# Revit family: Electronics -Communication_Urmet_1760-6
name_source: partatom
category: Apparecchi elettrici
revit_build: Autodesk Revit 2017 (Build: 20190508_0315(x64)
units: mm (PartAtom-declared; Revit-internal decimal feet)

## family parameters
Condiviso = No
Host = Superficie
Mantenere orientamento annotazione = No
Punto di calcolo locali = No
Quota connettore circolare = Usa diametro
Taglio con vuoti quando caricato = No
Tipo di parte = Normale

## types (1)
- Electronics -Communication_Urmet_1760-6
    Additional led signalizations = 0
    Audio or Audio/Video system = Audio/video
    Auto-insertion function and scrolling of CCTV cameras = Sì
    Automatic door opening function = Sì
    Auxiliary antenna for Hearing impaired people = Sì
    Brand url = https://www.urmet.com
    Call forwarding = Yes, with optional device
    Codice assieme = 1760/6
    Color = White RAL9003
    Combined Nomenclature Code = 8517691000
    Compatibility with Alexa = No
    Data-sheet: = http://qrcode.urmet.com
    Date of publishing = 2023-02-01
    Descrizione = VIDEO DOOR PHONE HANDS-FREE
VIDEO HOUSEPHONE 4,3'’ HANDSFREE 2VOICE WHITE
    Design country = Italy
    Dimensions (LxHxP) = 130 x 160 x 26 mm
    Display Dimensions = 5’’ IPS-LCD
    Display Format = 16:9
    Display resolution (pixel) = 800 x 480
    EAN Product Code = 8021156069781
    Edition number = 1
    Finishing = Gloss
    Gate door opening = Sì
    Gesture = Sì
    Handset /Hands free = Hands free
    Home automation Yokis buttons = -
    Humidity range (%) = 95%
    IFC Classification = Electrical Element
    IK Grade = -
    IP Grade = 30
    Incoming floor call = Sì
    Installation = Surface mounting, flush mounting or table mounting (with optional accessory)
    Installation instructions = http://qrcode.urmet.com
    Installation on 503 flush and 60 mm diameter round boxes = Sì
    Main led signalizations = 5
    Manufacturer country = China
    Masterformat 2014 Code = 27 51 23.30
    Masterformat 2014 Description = Residential Intercommunications and Program Systems
    Material main = Plastic
    Modello = VOG5
    N. od terminal blocks = 6
    NBS Reference Code = 16-02-43
    NBS Reference Description = Intercom Remote Handsets
    Nominal height = 160 mm  [stored 0.524934 ft]
    Nominal width = 130 mm  [stored 0.426509 ft]
    Number of Touch buttons = 8
    Number of mechanical Pushbuttons = 0
    OmniClass Code = 23-37 23 17 13
    OmniClass Description = Door Entry Telephones
    Outgoing intercom calls = 3
    Pedestrian door opening = Sì
    Power consumption: = http://qrcode.urmet.com
    Predisposition for external optional ringer = Sì
    Product Guide: = http://qrcode.urmet.com
    Product SKU = 1760-6
    Product certification = http://qrcode.urmet.com
    Product url = http://qrcode.urmet.com
    Produttore = Urmet S.p.A.
Urmet S.p.A.
    Proprietary voice controls = No
    Prospetto di default = 1219 mm
    Remote relay activations = 1
    Ringing off (mute) function = Sì
    Ringing volume regulation = Sì
    Selectable ringtone for external calls and floor call = Sì
    Sustainability Performance = RAEE/WEEE compliant
    Switchboard call = Sì
    System name = 2Voice
2Voice
2Voice
2Voice
    System technology = 2 wires
    Technical description = http://qrcode.urmet.com
    Temperature range (°C) = -5/50
    Terminal block labels = S-  S+  2xCP  2xLINE IN
    Touch Display = Sì
    Type image = http://qrcode.urmet.com
    UE Conformity Declaration: = http://qrcode.urmet.com
    UNSPSC Code = 43221525
    URL = https://www.urmet.com
    Uniclass 1.4 Code = L7632
    Uniclass 1.4 Description = Intercom systems
    Uniclass 2.0 Code = PR-16-02-43
    Uniclass 2.0 Description = Intercom Remote Handsets
    Uniclass 2015 Code = Pr_75_75_27_43
    Uniclass 2015 Name = Intercom remote handsets
    Uniformat II Code = D5030
    Uniformat II Description = Communications & Security
    Video color regulation = Sì
    Video contrast regulation = Sì
    Video luminosity regulation = Sì
    Voltage = Low voltage (<50Vdc)
    Weight net = 0.60 kg
    Wiring = 2 wires

note: [stored X ft] marks values corroborated as IEEE doubles in the binary element streams (Revit-internal decimal feet)

## geometry (parser evidence)
native form markers: Sweep x2
no freeform markers — native parametric forms only
